# Revit family: Street Light - Antique
name_source: partatom
category: Lighting Fixtures
revit_build: Autodesk Revit Architecture 2012 (Build: 20110210_1515)
units: mm (PartAtom-declared; Revit-internal decimal feet)

## types (9) — shared parameters
Assembly Code = D5020280
Color Filter = 16777215
Dimming Lamp Color Temperature Shift = <None>
Light Source Symbol Size = 2' - 0"
Load Classification = Lighting - Exterior
Shade Material = Glass - Frosted
Stand Material = Metal - Paint Finish - Dark Gray, Matte

## per-type parameters (varying)
| type | Apparent Load | Ballast Number of Poles | Ballast Voltage | Height | Lamp | Wattage Comments |
| 400W Halogen - 120V | 400 VA | 1 | 120 V | 14' - 11" | T-3 | 400 |
| 250W Sodium - 120V | 250 VA | 1 | 120 V | 16' - 0" | ET-18 | 250 |
| 250W Halogen - 120V | 250 VA | 1 | 120 V | 14' - 11" | T-4 | 250 |
| 250W Halogen - 277V | 250 VA | 1 | 277 V | 14' - 11" | T-4 | 250 |
| 250W Halogen - 480V | 250 VA | 3 | 480 V | 14' - 11" | T-4 | 250 |
| 250W Sodium - 277V | 250 VA | 1 | 277 V | 16' - 0" | ET-18 | 250 |
| 250W Sodium - 480V | 250 VA | 3 | 480 V | 16' - 0" | ET-18 | 250 |
| 400W Halogen - 277V | 400 VA | 1 | 277 V | 14' - 11" | T-3 | 400 |
| 400W Halogen - 480V | 400 VA | 3 | 480 V | 14' - 11" | T-3 | 400 |

## geometry (parser evidence)
native form markers: Sweep x1
no freeform markers — native parametric forms only
